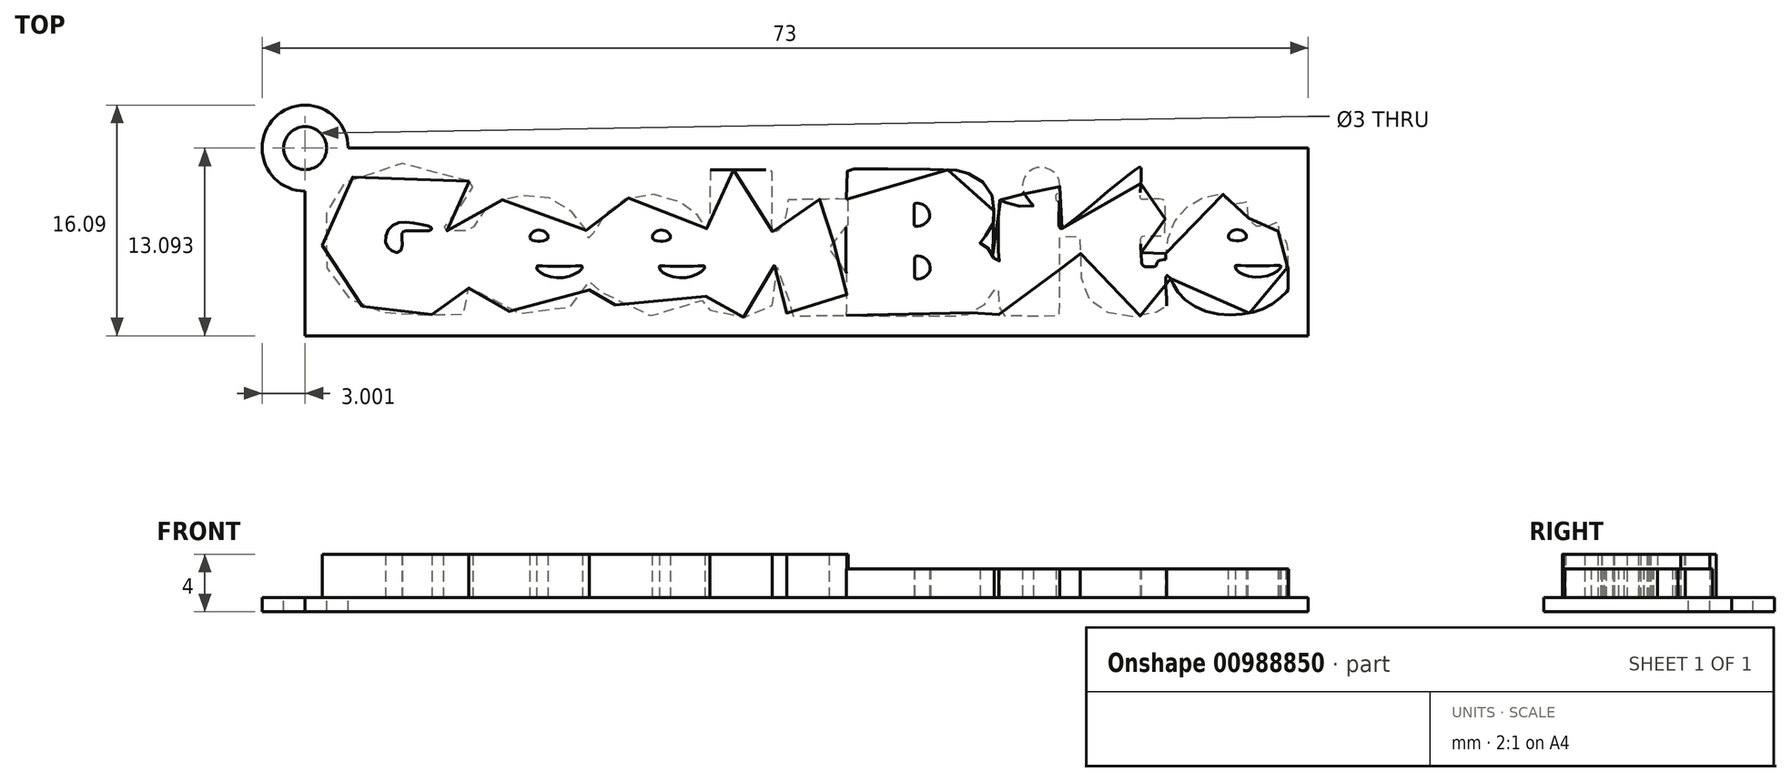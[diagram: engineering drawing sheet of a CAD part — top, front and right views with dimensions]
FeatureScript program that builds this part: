
annotation { "Feature Type Name" : "Feature", "Feature Type Description" : "" }
export const myFeature = defineFeature(function(context is Context, id is Id, definition is map)
    precondition{}
    {
        {
            var Q0;
            Q0=qCreatedBy(makeId("Top.planeOp"),FACE);
            var sketch = newSketch(context, id + "F0", { "sketchPlane" : qUnion([Q0])});
            skSolve(sketch);
        }
        {
            var Q0;
            Q0=qCreatedBy(makeId("Top.planeOp"),FACE);
            var sketch = newSketch(context, id + "F1", { "sketchPlane" : qUnion([Q0])});
            skFitSpline(sketch, "E0", {"points": [v(-21.14, 3.59) * mm, v(-25.99, 4.84) * mm, v(-29.67, 3.6) * mm, v(-30.66, 2.48) * mm, v(-31.12, 1.39) * mm, v(-31.28, -1.8) * mm, v(-30.2, -3.88) * mm, v(-29.43, -4.64) * mm, v(-28.18, -5.28) * mm, v(-26.93, -5.58) * mm, v(-25.79, -5.69) * mm, v(-23.48, -5.71) * mm, v(-21.77, -5.68) * mm, v(-21.28, -5.64) * mm, v(-21.18, -5.25) * mm, v(-21.16, -3.7) * mm, v(-21.04, -3.43) * mm, v(-20.8, -3.54) * mm, v(-20.46, -4.04) * mm, v(-19.26, -5.14) * mm, v(-16.76, -5.7) * mm, v(-14.06, -5.16) * mm, v(-12.74, -3.97) * mm, v(-12.75, -3.94) * mm, v(-12.75, -3.28) * mm, v(-12.72, -3.18) * mm, v(-12.43, -3.2) * mm, v(-12.28, -3.62) * mm, v(-10.67, -5.19) * mm, v(-6.8, -5.67) * mm, v(-4.75, -4.6) * mm, v(-4.49, -4.33) * mm, v(-4.33, -4.49) * mm, v(-4.35, -5.45) * mm, v(-4.33, -5.75) * mm, v(-4.08, -5.82) * mm, v(-0.24, -5.86) * mm, v(-0.08, -5.79) * mm, v(0, -5.58) * mm, v(0.07, -2.33) * mm, v(0.18, -2.3) * mm, v(0.42, -2.47) * mm, v(0.68, -2.84) * mm, v(0.95, -3.71) * mm, v(1.03, -5.34) * mm, v(1.02, -5.68) * mm, v(1.32, -5.8) * mm, v(5.1, -5.83) * mm, v(5.18, -5.77) * mm, v(5.21, -2.94) * mm, v(5.16, -2.8) * mm, v(4.49, -1.78) * mm, v(3.96, -1.08) * mm, v(4.02, -1) * mm, v(5.28, 0.56) * mm, v(5.31, 0.66) * mm, v(5.32, 2.28) * mm, v(5.28, 2.34) * mm, v(1.2, 2.3) * mm, v(1.1, 2.24) * mm, v(0.83, 0.78) * mm, v(0.12, 0) * mm, v(0, 0.29) * mm, v(0, 4.23) * mm, v(-0.26, 4.4) * mm, v(-4.24, 4.4) * mm, v(-4.3, 4.4) * mm, v(-4.33, 4.21) * mm, v(-4.43, 0.34) * mm, v(-4.54, 0.27) * mm, v(-5, 0.97) * mm, v(-7.36, 2.52) * mm, v(-11.04, 1.9) * mm, v(-12.55, -0.18) * mm, v(-12.71, -0.43) * mm, v(-12.92, -0.26) * mm, v(-13, 0.17) * mm, v(-15.03, 2.22) * mm, v(-18.2, 2.46) * mm, v(-20.15, 1.5) * mm, v(-20.91, 0.23) * mm, v(-21.07, 0.14) * mm, v(-22.79, 0.13) * mm, v(-22.95, 0.2) * mm, v(-22.88, 0.37) * mm, v(-20.94, 3.04) * mm, v(-20.9, 3.34) * mm, v(-21.14, 3.59) * mm]});
            skFitSpline(sketch, "E1", {"points": [v(-25.55, 0.14) * mm, v(-25.78, 0.06) * mm, v(-25.83, -0.13) * mm, v(-25.9, -1.24) * mm, v(-26.5, -1.29) * mm, v(-26.98, -0.53) * mm, v(-26.47, 0.53) * mm, v(-24.95, 0.67) * mm, v(-23.8, 0.37) * mm, v(-23.75, 0.28) * mm, v(-23.9, 0.16) * mm, v(-25.55, 0.14) * mm]});
            skFitSpline(sketch, "E2", {"points": [v(-16.85, -0.44) * mm, v(-15.77, -0.49) * mm, v(-15.68, -0.13) * mm, v(-16.23, 0.2) * mm, v(-16.78, -0.05) * mm, v(-16.85, -0.44) * mm]});
            skFitSpline(sketch, "E3", {"points": [v(-16.26, -2.3) * mm, v(-14.83, -2.35) * mm, v(-13.42, -2.3) * mm, v(-13.25, -2.34) * mm, v(-13.37, -2.62) * mm, v(-14.9, -3.14) * mm, v(-16.36, -2.6) * mm, v(-16.4, -2.33) * mm, v(-16.26, -2.3) * mm]});
            skFitSpline(sketch, "E4", {"points": [v(-8.3, -0.44) * mm, v(-7.22, -0.49) * mm, v(-7.13, -0.13) * mm, v(-7.68, 0.2) * mm, v(-8.23, -0.05) * mm, v(-8.3, -0.44) * mm]});
            skFitSpline(sketch, "E5", {"points": [v(-7.71, -2.3) * mm, v(-6.29, -2.35) * mm, v(-4.87, -2.3) * mm, v(-4.7, -2.34) * mm, v(-4.82, -2.62) * mm, v(-6.36, -3.14) * mm, v(-7.81, -2.6) * mm, v(-7.85, -2.33) * mm, v(-7.71, -2.3) * mm]});
            skSolve(sketch);
        }
        {
            var Q0;
            Q0 = qSketchRegion(id + "F1", true);
            extrude(context, id + "F2", {"entities" : qUnion([Q0]), "depth" : 3 * mm, "offsetDistance" : 25 * mm});
        }
        {
            var Q0;
            Q0=qCreatedBy(makeId("Top.planeOp"),FACE);
            var sketch = newSketch(context, id + "F3", { "sketchPlane" : qUnion([Q0])});
            skFitSpline(sketch, "E6", {"points": [v(5.51, 4.42) * mm, v(5.27, 4.36) * mm, v(5.22, 4.18) * mm, v(5.18, -5.6) * mm, v(5.19, -5.76) * mm, v(5.3, -5.78) * mm, v(13.1, -5.8) * mm, v(13.36, -5.77) * mm, v(14.67, -5.14) * mm, v(15.5, -4.02) * mm, v(15.5, -3.93) * mm, v(15.74, -3.9) * mm, v(15.81, -3.94) * mm, v(15.82, -5.65) * mm, v(15.92, -5.76) * mm, v(19.94, -5.78) * mm, v(20.05, -5.76) * mm, v(20.07, -5.6) * mm, v(20.08, -0.46) * mm, v(20.1, -0.3) * mm, v(20.2, -0.26) * mm, v(21.3, -0.23) * mm, v(21.44, -0.25) * mm, v(21.52, -1.18) * mm, v(21.75, -3.96) * mm, v(23.44, -5.56) * mm, v(26.44, -5.67) * mm, v(27.52, -5.14) * mm, v(27.54, -5.08) * mm, v(27.47, -3.13) * mm, v(27.53, -2.97) * mm, v(27.73, -3.07) * mm, v(28.25, -4.04) * mm, v(30.17, -5.44) * mm, v(33, -5.65) * mm, v(34.99, -4.9) * mm, v(36, -4.02) * mm, v(36.02, -3.95) * mm, v(36.03, -2.56) * mm, v(36, -2.41) * mm, v(35.85, -2.31) * mm, v(36, -2.2) * mm, v(36.01, -2.12) * mm, v(36.02, -1.3) * mm, v(35.94, -0.73) * mm, v(35.9, -0.58) * mm, v(35.39, -0.07) * mm, v(35.33, 0.23) * mm, v(35.4, 0.54) * mm, v(35.3, 0.75) * mm, v(35.01, 0.66) * mm, v(34.75, 0.48) * mm, v(33.84, 0.44) * mm, v(33.24, 1.04) * mm, v(33.2, 1.91) * mm, v(33.14, 2.18) * mm, v(32.91, 2.09) * mm, v(32.12, 2.02) * mm, v(31.63, 2.46) * mm, v(31.52, 2.68) * mm, v(31.33, 2.66) * mm, v(29.92, 2.34) * mm, v(27.83, 0.34) * mm, v(27.47, -1.8) * mm, v(27.47, -1.86) * mm, v(27.05, -1.92) * mm, v(26.84, -2.17) * mm, v(26.75, -2.33) * mm, v(26, -2.35) * mm, v(25.8, -2.1) * mm, v(25.73, -0.52) * mm, v(25.75, -0.32) * mm, v(26.02, -0.22) * mm, v(27.22, -0.22) * mm, v(27.37, -0.2) * mm, v(27.41, -0.06) * mm, v(27.44, 1.89) * mm, v(27.43, 2.14) * mm, v(27.22, 2.33) * mm, v(25.88, 2.31) * mm, v(25.77, 2.34) * mm, v(25.7, 2.46) * mm, v(25.77, 4.35) * mm, v(25.72, 4.55) * mm, v(25.57, 4.55) * mm, v(20.37, 0.38) * mm, v(20.14, 0.3) * mm, v(20.03, 0.42) * mm, v(20.05, 2.1) * mm, v(19.99, 2.23) * mm, v(19.88, 2.21) * mm, v(19.84, 2.66) * mm, v(19.95, 2.75) * mm, v(20, 3.77) * mm, v(18.85, 4.56) * mm, v(17.84, 4.18) * mm, v(17.46, 3.28) * mm, v(17.67, 2.52) * mm, v(18.12, 2.09) * mm, v(18.24, 1.92) * mm, v(18.13, 1.83) * mm, v(16.75, 1.93) * mm, v(16.16, 2.2) * mm, v(15.93, 2.3) * mm, v(15.85, 2.15) * mm, v(15.85, -1.78) * mm, v(15.9, -1.95) * mm, v(15.76, -1.98) * mm, v(15.51, -1.9) * mm, v(15.32, -1.28) * mm, v(14.63, -0.84) * mm, v(14.51, -0.7) * mm, v(14.58, -0.53) * mm, v(15.3, 0.29) * mm, v(15.48, 1.32) * mm, v(15.4, 2.43) * mm, v(14.67, 3.54) * mm, v(13.4, 4.24) * mm, v(12.33, 4.39) * mm, v(5.51, 4.42) * mm]});
            skFitSpline(sketch, "E7", {"points": [v(9.91, 1.85) * mm, v(9.92, 0.65) * mm, v(9.99, 0.46) * mm, v(10.55, 0.56) * mm, v(11, 1.2) * mm, v(10.57, 1.93) * mm, v(9.99, 2.04) * mm, v(9.91, 1.85) * mm]});
            skFitSpline(sketch, "E8", {"points": [v(9.95, -1.82) * mm, v(9.96, -3.03) * mm, v(10.02, -3.2) * mm, v(10.58, -3.11) * mm, v(11.04, -2.47) * mm, v(10.6, -1.74) * mm, v(10.02, -1.63) * mm, v(9.95, -1.82) * mm]});
            skFitSpline(sketch, "E9", {"points": [v(31.9, -0.41) * mm, v(32.97, -0.46) * mm, v(33.07, -0.1) * mm, v(32.51, 0.23) * mm, v(31.96, -0.01) * mm, v(31.9, -0.41) * mm]});
            skFitSpline(sketch, "E10", {"points": [v(32.48, -2.28) * mm, v(33.91, -2.31) * mm, v(35.32, -2.27) * mm, v(35.5, -2.3) * mm, v(35.38, -2.58) * mm, v(33.84, -3.1) * mm, v(32.39, -2.56) * mm, v(32.34, -2.3) * mm, v(32.48, -2.28) * mm]});
            skSolve(sketch);
        }
        {
            var Q0;
            Q0 = qSketchRegion(id + "F3", true);
            extrude(context, id + "F4", {"entities" : qUnion([Q0]), "operationType" : NewBodyOperationType.ADD, "depth" : 2 * mm, "offsetDistance" : 25 * mm});
        }
        {
            var Q0;
            Q0=qCreatedBy(makeId("Top.planeOp"),FACE);
            var sketch = newSketch(context, id + "F5", { "sketchPlane" : qUnion([Q0])});
            skLineSegment(sketch, "E11.bottom", {"start": v(-32.59, 5.9) * mm, "end": v(37.41, 5.9) * mm});
            skLineSegment(sketch, "E11.top", {"start": v(-32.59, -7.19) * mm, "end": v(37.41, -7.19) * mm});
            skLineSegment(sketch, "E11.left", {"start": v(-32.59, 5.9) * mm, "end": v(-32.59, -7.19) * mm});
            skLineSegment(sketch, "E11.right", {"start": v(37.41, 5.9) * mm, "end": v(37.41, -7.19) * mm});
            skCircle(sketch, "E12", {"center": v(-32.59, 5.9) * mm, "radius": 3 * mm});
            skSolve(sketch);
        }
        {
            var Q0;
            Q0 = qSketchRegion(id + "F5", true);
            extrude(context, id + "F6", {"entities" : qUnion([Q0]), "operationType" : NewBodyOperationType.ADD, "oppositeDirection" : true, "depth" : 1 * mm, "offsetDistance" : 25 * mm});
        }
        {
            var Q0;
            Q0=qCreatedBy(makeId("Top.planeOp"),FACE);
            var sketch = newSketch(context, id + "F7", { "sketchPlane" : qUnion([Q0])});
            skCircle(sketch, "E13", {"center": v(-32.59, 5.9) * mm, "radius": 1.5 * mm});
            skSolve(sketch);
        }
        {
            var Q0;
            Q0 = qSketchRegion(id + "F7", true);
            extrude(context, id + "F8", {"entities" : qUnion([Q0]), "operationType" : NewBodyOperationType.REMOVE, "oppositeDirection" : true, "depth" : 25 * mm, "offsetDistance" : 25 * mm});
        }
    });
